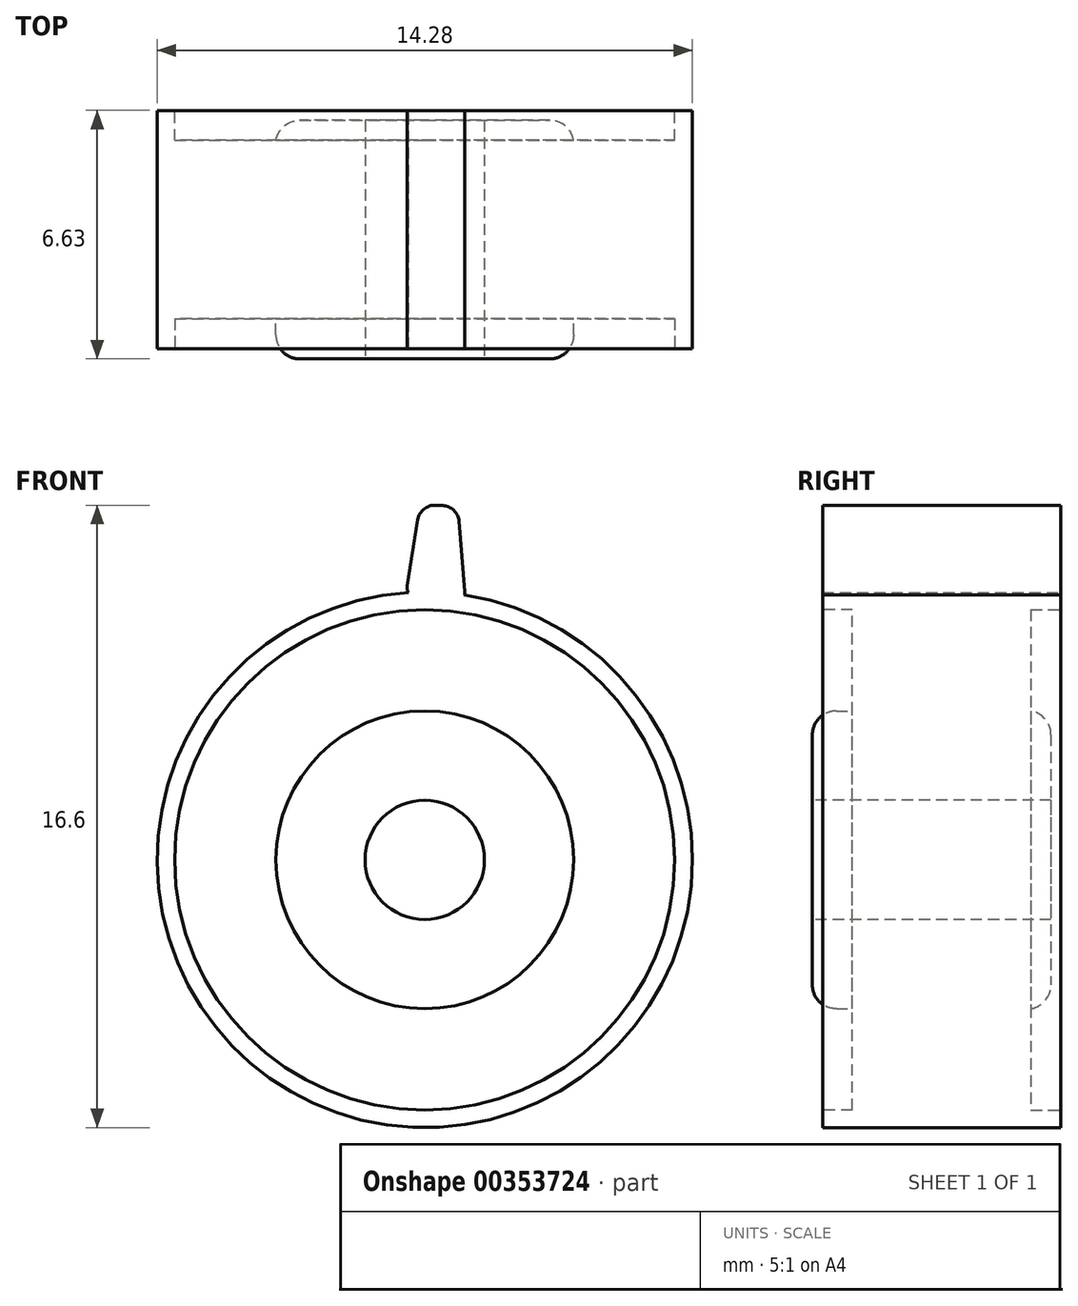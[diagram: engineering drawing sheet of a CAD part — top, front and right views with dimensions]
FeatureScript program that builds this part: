
annotation { "Feature Type Name" : "Feature", "Feature Type Description" : "" }
export const myFeature = defineFeature(function(context is Context, id is Id, definition is map)
    precondition{}
    {
        {
            var Q0;
            Q0=qCreatedBy(makeId("Front.planeOp"),FACE);
            var sketch = newSketch(context, id + "F0", { "sketchPlane" : qUnion([Q0])});
            skCircle(sketch, "E0", {"center": v(0, 0) * mm, "radius": 7.14 * mm});
            skSolve(sketch);
        }
        {
            var Q0;
            Q0 = qSketchRegion(id + "F0", true);
            extrude(context, id + "F1", {"entities" : qUnion([Q0]), "depth" : 6.35 * mm, "symmetric" : true});
        }
        {
            var Q0;
            Q0=makeQuery(id+"F1.opExtrude","CAP_FACE",FACE,{"disambiguationData":[OSD([sQuery(id+"F0.wireOp",EDGE,"E0")])],"isStart":false});
            var sketch = newSketch(context, id + "F2", { "sketchPlane" : qUnion([Q0])});
            skLineSegment(sketch, "E1", {"start": v(-0.5, 7.13) * mm, "end": v(1.08, 7.06) * mm});
            skLineSegment(sketch, "E2", {"start": v(-0.5, 7.13) * mm, "end": v(-0.12, 9.48) * mm});
            skLineSegment(sketch, "E3", {"start": v(-0.12, 9.48) * mm, "end": v(0.88, 9.43) * mm});
            skLineSegment(sketch, "E4", {"start": v(0.88, 9.43) * mm, "end": v(1.08, 7.06) * mm});
            skSolve(sketch);
        }
        {
            var Q0;
            Q0 = qSketchRegion(id + "F2", true);
            extrude(context, id + "F3", {"entities" : qUnion([Q0]), "operationType" : NewBodyOperationType.ADD, "oppositeDirection" : true, "depth" : 6.35 * mm});
        }
        {
            var Q0;
            Q0=makeQuery(id+"F3.opExtrude","SWEPT_EDGE",EDGE,{"disambiguationData":[OSD([sQuery(id+"F2.wireOp",EDGE,"E2"),sQuery(id+"F2.wireOp",EDGE,"E3")])]});
            var Q1;
            Q1=makeQuery(id+"F3.opExtrude","SWEPT_EDGE",EDGE,{"disambiguationData":[OSD([sQuery(id+"F2.wireOp",EDGE,"E3"),sQuery(id+"F2.wireOp",EDGE,"E4")])]});
            fillet(context, id + "F4", {"entities" : qUnion([Q0, Q1]), "radius" : 0.46 * mm, "tangentPropagation" : true, "allowEdgeOverflow" : false});
        }
        {
            var Q0;
            Q0=makeQuery(id+"F3.opExtrude","SWEPT_EDGE",EDGE,{"disambiguationData":[OSD([sQuery(id+"F0.wireOp",EDGE,"E0"),sQuery(id+"F2.wireOp",EDGE,"E1"),sQuery(id+"F2.wireOp",EDGE,"E2")])]});
            var Q1;
            Q1=makeQuery(id+"F3.opExtrude","SWEPT_EDGE",EDGE,{"disambiguationData":[OSD([sQuery(id+"F0.wireOp",EDGE,"E0"),sQuery(id+"F2.wireOp",EDGE,"E1"),sQuery(id+"F2.wireOp",EDGE,"E4")])]});
            fillet(context, id + "F5", {"entities" : qUnion([Q0, Q1]), "radius" : 0.25 * mm, "tangentPropagation" : true, "allowEdgeOverflow" : false});
        }
        {
            var Q0;
            {var subQ0=sQuery(id+"F2.wireOp",EDGE,"E4");var subQ1=sQuery(id+"F2.wireOp",EDGE,"E3");var subQ2=sQuery(id+"F2.wireOp",EDGE,"E2");var subQ3=sQuery(id+"F2.wireOp",EDGE,"E1");Q0=makeQuery(id+"F0Lkjj2sYBY11f2_1.19.F3.boolean.opBoolean","MERGE",FACE,{"derivedFrom":[makeQuery(id+"F0Lkjj2sYBY11f2_1.18.F3.boolean.opBoolean","MERGE",FACE,{"derivedFrom":[makeQuery(id+"F0Lkjj2sYBY11f2_1.17.F3.boolean.opBoolean","MERGE",FACE,{"derivedFrom":[makeQuery(id+"F0Lkjj2sYBY11f2_1.16.F3.boolean.opBoolean","MERGE",FACE,{"derivedFrom":[makeQuery(id+"F0Lkjj2sYBY11f2_1.15.F3.boolean.opBoolean","MERGE",FACE,{"derivedFrom":[makeQuery(id+"F0Lkjj2sYBY11f2_1.14.F3.boolean.opBoolean","MERGE",FACE,{"derivedFrom":[makeQuery(id+"F0Lkjj2sYBY11f2_1.13.F3.boolean.opBoolean","MERGE",FACE,{"derivedFrom":[makeQuery(id+"F0Lkjj2sYBY11f2_1.12.F3.boolean.opBoolean","MERGE",FACE,{"derivedFrom":[makeQuery(id+"F0Lkjj2sYBY11f2_1.11.F3.boolean.opBoolean","MERGE",FACE,{"derivedFrom":[makeQuery(id+"F0Lkjj2sYBY11f2_1.10.F3.boolean.opBoolean","MERGE",FACE,{"derivedFrom":[makeQuery(id+"F0Lkjj2sYBY11f2_1.9.F3.boolean.opBoolean","MERGE",FACE,{"derivedFrom":[makeQuery(id+"F0Lkjj2sYBY11f2_1.8.F3.boolean.opBoolean","MERGE",FACE,{"derivedFrom":[makeQuery(id+"F0Lkjj2sYBY11f2_1.7.F3.boolean.opBoolean","MERGE",FACE,{"derivedFrom":[makeQuery(id+"F0Lkjj2sYBY11f2_1.6.F3.boolean.opBoolean","MERGE",FACE,{"derivedFrom":[makeQuery(id+"F0Lkjj2sYBY11f2_1.5.F3.boolean.opBoolean","MERGE",FACE,{"derivedFrom":[makeQuery(id+"F0Lkjj2sYBY11f2_1.4.F3.boolean.opBoolean","MERGE",FACE,{"derivedFrom":[makeQuery(id+"F0Lkjj2sYBY11f2_1.3.F3.boolean.opBoolean","MERGE",FACE,{"derivedFrom":[makeQuery(id+"F0Lkjj2sYBY11f2_1.2.F3.boolean.opBoolean","MERGE",FACE,{"derivedFrom":[makeQuery(id+"F0Lkjj2sYBY11f2_1.1.F3.boolean.opBoolean","MERGE",FACE,{"derivedFrom":[makeQuery(id+"F3.boolean.opBoolean","MERGE",FACE,{"derivedFrom":[makeQuery(id+"F1.opExtrude","CAP_FACE",FACE,{"disambiguationData":[OSD([sQuery(id+"F0.wireOp",EDGE,"E0")])],"isStart":false}),makeQuery(id+"F3.opExtrude","CAP_FACE",FACE,{"disambiguationData":[OSD([subQ3,subQ2,subQ1,subQ0])],"isStart":true})]}),makeQuery(id+"F0Lkjj2sYBY11f2_1.1.F3.opExtrude","CAP_FACE",FACE,{"disambiguationData":[OSD([subQ3,subQ2,subQ1,subQ0])],"isStart":true})]}),makeQuery(id+"F0Lkjj2sYBY11f2_1.2.F3.opExtrude","CAP_FACE",FACE,{"disambiguationData":[OSD([subQ3,subQ2,subQ1,subQ0])],"isStart":true})]}),makeQuery(id+"F0Lkjj2sYBY11f2_1.3.F3.opExtrude","CAP_FACE",FACE,{"disambiguationData":[OSD([subQ3,subQ2,subQ1,subQ0])],"isStart":true})]}),makeQuery(id+"F0Lkjj2sYBY11f2_1.4.F3.opExtrude","CAP_FACE",FACE,{"disambiguationData":[OSD([subQ3,subQ2,subQ1,subQ0])],"isStart":true})]}),makeQuery(id+"F0Lkjj2sYBY11f2_1.5.F3.opExtrude","CAP_FACE",FACE,{"disambiguationData":[OSD([subQ3,subQ2,subQ1,subQ0])],"isStart":true})]}),makeQuery(id+"F0Lkjj2sYBY11f2_1.6.F3.opExtrude","CAP_FACE",FACE,{"disambiguationData":[OSD([subQ3,subQ2,subQ1,subQ0])],"isStart":true})]}),makeQuery(id+"F0Lkjj2sYBY11f2_1.7.F3.opExtrude","CAP_FACE",FACE,{"disambiguationData":[OSD([subQ3,subQ2,subQ1,subQ0])],"isStart":true})]}),makeQuery(id+"F0Lkjj2sYBY11f2_1.8.F3.opExtrude","CAP_FACE",FACE,{"disambiguationData":[OSD([subQ3,subQ2,subQ1,subQ0])],"isStart":true})]}),makeQuery(id+"F0Lkjj2sYBY11f2_1.9.F3.opExtrude","CAP_FACE",FACE,{"disambiguationData":[OSD([subQ3,subQ2,subQ1,subQ0])],"isStart":true})]}),makeQuery(id+"F0Lkjj2sYBY11f2_1.10.F3.opExtrude","CAP_FACE",FACE,{"disambiguationData":[OSD([subQ3,subQ2,subQ1,subQ0])],"isStart":true})]}),makeQuery(id+"F0Lkjj2sYBY11f2_1.11.F3.opExtrude","CAP_FACE",FACE,{"disambiguationData":[OSD([subQ3,subQ2,subQ1,subQ0])],"isStart":true})]}),makeQuery(id+"F0Lkjj2sYBY11f2_1.12.F3.opExtrude","CAP_FACE",FACE,{"disambiguationData":[OSD([subQ3,subQ2,subQ1,subQ0])],"isStart":true})]}),makeQuery(id+"F0Lkjj2sYBY11f2_1.13.F3.opExtrude","CAP_FACE",FACE,{"disambiguationData":[OSD([subQ3,subQ2,subQ1,subQ0])],"isStart":true})]}),makeQuery(id+"F0Lkjj2sYBY11f2_1.14.F3.opExtrude","CAP_FACE",FACE,{"disambiguationData":[OSD([subQ3,subQ2,subQ1,subQ0])],"isStart":true})]}),makeQuery(id+"F0Lkjj2sYBY11f2_1.15.F3.opExtrude","CAP_FACE",FACE,{"disambiguationData":[OSD([subQ3,subQ2,subQ1,subQ0])],"isStart":true})]}),makeQuery(id+"F0Lkjj2sYBY11f2_1.16.F3.opExtrude","CAP_FACE",FACE,{"disambiguationData":[OSD([subQ3,subQ2,subQ1,subQ0])],"isStart":true})]}),makeQuery(id+"F0Lkjj2sYBY11f2_1.17.F3.opExtrude","CAP_FACE",FACE,{"disambiguationData":[OSD([subQ3,subQ2,subQ1,subQ0])],"isStart":true})]}),makeQuery(id+"F0Lkjj2sYBY11f2_1.18.F3.opExtrude","CAP_FACE",FACE,{"disambiguationData":[OSD([subQ3,subQ2,subQ1,subQ0])],"isStart":true})]}),makeQuery(id+"F0Lkjj2sYBY11f2_1.19.F3.opExtrude","CAP_FACE",FACE,{"disambiguationData":[OSD([subQ3,subQ2,subQ1,subQ0])],"isStart":true})]});}
            var sketch = newSketch(context, id + "F6", { "sketchPlane" : qUnion([Q0])});
            skCircle(sketch, "E5", {"center": v(0, 0) * mm, "radius": 6.67 * mm});
            skSolve(sketch);
        }
        {
            var Q0;
            Q0 = qSketchRegion(id + "F6", true);
            extrude(context, id + "F7", {"entities" : qUnion([Q0]), "operationType" : NewBodyOperationType.REMOVE, "oppositeDirection" : true, "depth" : 1.59 * mm, "symmetric" : true});
        }
        {
            var Q0;
            Q0=makeQuery(id+"F7.boolean.opBoolean","COPY",FACE,{"derivedFrom":makeQuery(id+"F7.opExtrude","CAP_FACE",FACE,{"disambiguationData":[OSD([sQuery(id+"F6.wireOp",EDGE,"E5")])],"isStart":false})});
            var sketch = newSketch(context, id + "F8", { "sketchPlane" : qUnion([Q0])});
            skCircle(sketch, "E6", {"center": v(0, 0) * mm, "radius": 3.97 * mm});
            skSolve(sketch);
        }
        {
            var Q0;
            Q0 = qSketchRegion(id + "F8", true);
            extrude(context, id + "F9", {"entities" : qUnion([Q0]), "operationType" : NewBodyOperationType.ADD, "depth" : 1.07 * mm});
        }
        {
            var Q0;
            Q0=makeQuery(id+"F9.opExtrude","CAP_EDGE",EDGE,{"disambiguationData":[OSD([sQuery(id+"F8.wireOp",EDGE,"E6")])],"isStart":false});
            fillet(context, id + "F10", {"entities" : qUnion([Q0]), "radius" : 0.64 * mm, "tangentPropagation" : true, "allowEdgeOverflow" : false});
        }
        {
            var Q0;
            {var subQ0=sQuery(id+"F2.wireOp",EDGE,"E4");var subQ1=sQuery(id+"F2.wireOp",EDGE,"E3");var subQ2=sQuery(id+"F2.wireOp",EDGE,"E2");var subQ3=sQuery(id+"F2.wireOp",EDGE,"E1");Q0=makeQuery(id+"F0Lkjj2sYBY11f2_1.19.F3.boolean.opBoolean","MERGE",FACE,{"derivedFrom":[makeQuery(id+"F0Lkjj2sYBY11f2_1.18.F3.boolean.opBoolean","MERGE",FACE,{"derivedFrom":[makeQuery(id+"F0Lkjj2sYBY11f2_1.17.F3.boolean.opBoolean","MERGE",FACE,{"derivedFrom":[makeQuery(id+"F0Lkjj2sYBY11f2_1.16.F3.boolean.opBoolean","MERGE",FACE,{"derivedFrom":[makeQuery(id+"F0Lkjj2sYBY11f2_1.15.F3.boolean.opBoolean","MERGE",FACE,{"derivedFrom":[makeQuery(id+"F0Lkjj2sYBY11f2_1.14.F3.boolean.opBoolean","MERGE",FACE,{"derivedFrom":[makeQuery(id+"F0Lkjj2sYBY11f2_1.13.F3.boolean.opBoolean","MERGE",FACE,{"derivedFrom":[makeQuery(id+"F0Lkjj2sYBY11f2_1.12.F3.boolean.opBoolean","MERGE",FACE,{"derivedFrom":[makeQuery(id+"F0Lkjj2sYBY11f2_1.11.F3.boolean.opBoolean","MERGE",FACE,{"derivedFrom":[makeQuery(id+"F0Lkjj2sYBY11f2_1.10.F3.boolean.opBoolean","MERGE",FACE,{"derivedFrom":[makeQuery(id+"F0Lkjj2sYBY11f2_1.9.F3.boolean.opBoolean","MERGE",FACE,{"derivedFrom":[makeQuery(id+"F0Lkjj2sYBY11f2_1.8.F3.boolean.opBoolean","MERGE",FACE,{"derivedFrom":[makeQuery(id+"F0Lkjj2sYBY11f2_1.7.F3.boolean.opBoolean","MERGE",FACE,{"derivedFrom":[makeQuery(id+"F0Lkjj2sYBY11f2_1.6.F3.boolean.opBoolean","MERGE",FACE,{"derivedFrom":[makeQuery(id+"F0Lkjj2sYBY11f2_1.5.F3.boolean.opBoolean","MERGE",FACE,{"derivedFrom":[makeQuery(id+"F0Lkjj2sYBY11f2_1.4.F3.boolean.opBoolean","MERGE",FACE,{"derivedFrom":[makeQuery(id+"F0Lkjj2sYBY11f2_1.3.F3.boolean.opBoolean","MERGE",FACE,{"derivedFrom":[makeQuery(id+"F0Lkjj2sYBY11f2_1.2.F3.boolean.opBoolean","MERGE",FACE,{"derivedFrom":[makeQuery(id+"F0Lkjj2sYBY11f2_1.1.F3.boolean.opBoolean","MERGE",FACE,{"derivedFrom":[makeQuery(id+"F3.boolean.opBoolean","MERGE",FACE,{"derivedFrom":[makeQuery(id+"F1.opExtrude","CAP_FACE",FACE,{"disambiguationData":[OSD([sQuery(id+"F0.wireOp",EDGE,"E0")])],"isStart":true}),makeQuery(id+"F3.opExtrude","CAP_FACE",FACE,{"disambiguationData":[OSD([subQ3,subQ2,subQ1,subQ0])],"isStart":false})]}),makeQuery(id+"F0Lkjj2sYBY11f2_1.1.F3.opExtrude","CAP_FACE",FACE,{"disambiguationData":[OSD([subQ3,subQ2,subQ1,subQ0])],"isStart":false})]}),makeQuery(id+"F0Lkjj2sYBY11f2_1.2.F3.opExtrude","CAP_FACE",FACE,{"disambiguationData":[OSD([subQ3,subQ2,subQ1,subQ0])],"isStart":false})]}),makeQuery(id+"F0Lkjj2sYBY11f2_1.3.F3.opExtrude","CAP_FACE",FACE,{"disambiguationData":[OSD([subQ3,subQ2,subQ1,subQ0])],"isStart":false})]}),makeQuery(id+"F0Lkjj2sYBY11f2_1.4.F3.opExtrude","CAP_FACE",FACE,{"disambiguationData":[OSD([subQ3,subQ2,subQ1,subQ0])],"isStart":false})]}),makeQuery(id+"F0Lkjj2sYBY11f2_1.5.F3.opExtrude","CAP_FACE",FACE,{"disambiguationData":[OSD([subQ3,subQ2,subQ1,subQ0])],"isStart":false})]}),makeQuery(id+"F0Lkjj2sYBY11f2_1.6.F3.opExtrude","CAP_FACE",FACE,{"disambiguationData":[OSD([subQ3,subQ2,subQ1,subQ0])],"isStart":false})]}),makeQuery(id+"F0Lkjj2sYBY11f2_1.7.F3.opExtrude","CAP_FACE",FACE,{"disambiguationData":[OSD([subQ3,subQ2,subQ1,subQ0])],"isStart":false})]}),makeQuery(id+"F0Lkjj2sYBY11f2_1.8.F3.opExtrude","CAP_FACE",FACE,{"disambiguationData":[OSD([subQ3,subQ2,subQ1,subQ0])],"isStart":false})]}),makeQuery(id+"F0Lkjj2sYBY11f2_1.9.F3.opExtrude","CAP_FACE",FACE,{"disambiguationData":[OSD([subQ3,subQ2,subQ1,subQ0])],"isStart":false})]}),makeQuery(id+"F0Lkjj2sYBY11f2_1.10.F3.opExtrude","CAP_FACE",FACE,{"disambiguationData":[OSD([subQ3,subQ2,subQ1,subQ0])],"isStart":false})]}),makeQuery(id+"F0Lkjj2sYBY11f2_1.11.F3.opExtrude","CAP_FACE",FACE,{"disambiguationData":[OSD([subQ3,subQ2,subQ1,subQ0])],"isStart":false})]}),makeQuery(id+"F0Lkjj2sYBY11f2_1.12.F3.opExtrude","CAP_FACE",FACE,{"disambiguationData":[OSD([subQ3,subQ2,subQ1,subQ0])],"isStart":false})]}),makeQuery(id+"F0Lkjj2sYBY11f2_1.13.F3.opExtrude","CAP_FACE",FACE,{"disambiguationData":[OSD([subQ3,subQ2,subQ1,subQ0])],"isStart":false})]}),makeQuery(id+"F0Lkjj2sYBY11f2_1.14.F3.opExtrude","CAP_FACE",FACE,{"disambiguationData":[OSD([subQ3,subQ2,subQ1,subQ0])],"isStart":false})]}),makeQuery(id+"F0Lkjj2sYBY11f2_1.15.F3.opExtrude","CAP_FACE",FACE,{"disambiguationData":[OSD([subQ3,subQ2,subQ1,subQ0])],"isStart":false})]}),makeQuery(id+"F0Lkjj2sYBY11f2_1.16.F3.opExtrude","CAP_FACE",FACE,{"disambiguationData":[OSD([subQ3,subQ2,subQ1,subQ0])],"isStart":false})]}),makeQuery(id+"F0Lkjj2sYBY11f2_1.17.F3.opExtrude","CAP_FACE",FACE,{"disambiguationData":[OSD([subQ3,subQ2,subQ1,subQ0])],"isStart":false})]}),makeQuery(id+"F0Lkjj2sYBY11f2_1.18.F3.opExtrude","CAP_FACE",FACE,{"disambiguationData":[OSD([subQ3,subQ2,subQ1,subQ0])],"isStart":false})]}),makeQuery(id+"F0Lkjj2sYBY11f2_1.19.F3.opExtrude","CAP_FACE",FACE,{"disambiguationData":[OSD([subQ3,subQ2,subQ1,subQ0])],"isStart":false})]});}
            var sketch = newSketch(context, id + "F11", { "sketchPlane" : qUnion([Q0])});
            skCircle(sketch, "E7", {"center": v(0, 0) * mm, "radius": 6.67 * mm});
            skSolve(sketch);
        }
        {
            var Q0;
            Q0 = qSketchRegion(id + "F11", true);
            extrude(context, id + "F12", {"entities" : qUnion([Q0]), "operationType" : NewBodyOperationType.REMOVE, "oppositeDirection" : true, "depth" : 1.59 * mm, "symmetric" : true});
        }
        {
            var Q0;
            Q0=makeQuery(id+"F12.boolean.opBoolean","COPY",FACE,{"derivedFrom":makeQuery(id+"F12.opExtrude","CAP_FACE",FACE,{"disambiguationData":[OSD([sQuery(id+"F11.wireOp",EDGE,"E7")])],"isStart":false})});
            var sketch = newSketch(context, id + "F13", { "sketchPlane" : qUnion([Q0])});
            skCircle(sketch, "E8", {"center": v(0, 0) * mm, "radius": 3.97 * mm});
            skSolve(sketch);
        }
        {
            var Q0;
            Q0 = qSketchRegion(id + "F13", true);
            extrude(context, id + "F14", {"entities" : qUnion([Q0]), "operationType" : NewBodyOperationType.ADD, "depth" : 1.07 * mm, "symmetric" : true});
        }
        {
            var Q0;
            Q0=makeQuery(id+"F14.opExtrude","CAP_EDGE",EDGE,{"disambiguationData":[OSD([sQuery(id+"F13.wireOp",EDGE,"E8")])],"isStart":false});
            fillet(context, id + "F15", {"entities" : qUnion([Q0]), "radius" : 0.64 * mm, "tangentPropagation" : true, "allowEdgeOverflow" : false});
        }
        {
            var Q0;
            Q0=makeQuery(id+"F14.opExtrude","CAP_FACE",FACE,{"disambiguationData":[OSD([sQuery(id+"F13.wireOp",EDGE,"E8")])],"isStart":false});
            var sketch = newSketch(context, id + "F16", { "sketchPlane" : qUnion([Q0])});
            skCircle(sketch, "E9", {"center": v(0, 0) * mm, "radius": 1.59 * mm});
            skSolve(sketch);
        }
        {
            var Q0;
            Q0 = qSketchRegion(id + "F16", true);
            extrude(context, id + "F17", {"entities" : qUnion([Q0]), "operationType" : NewBodyOperationType.REMOVE, "depth" : 25.4 * mm, "symmetric" : true});
        }
    });
